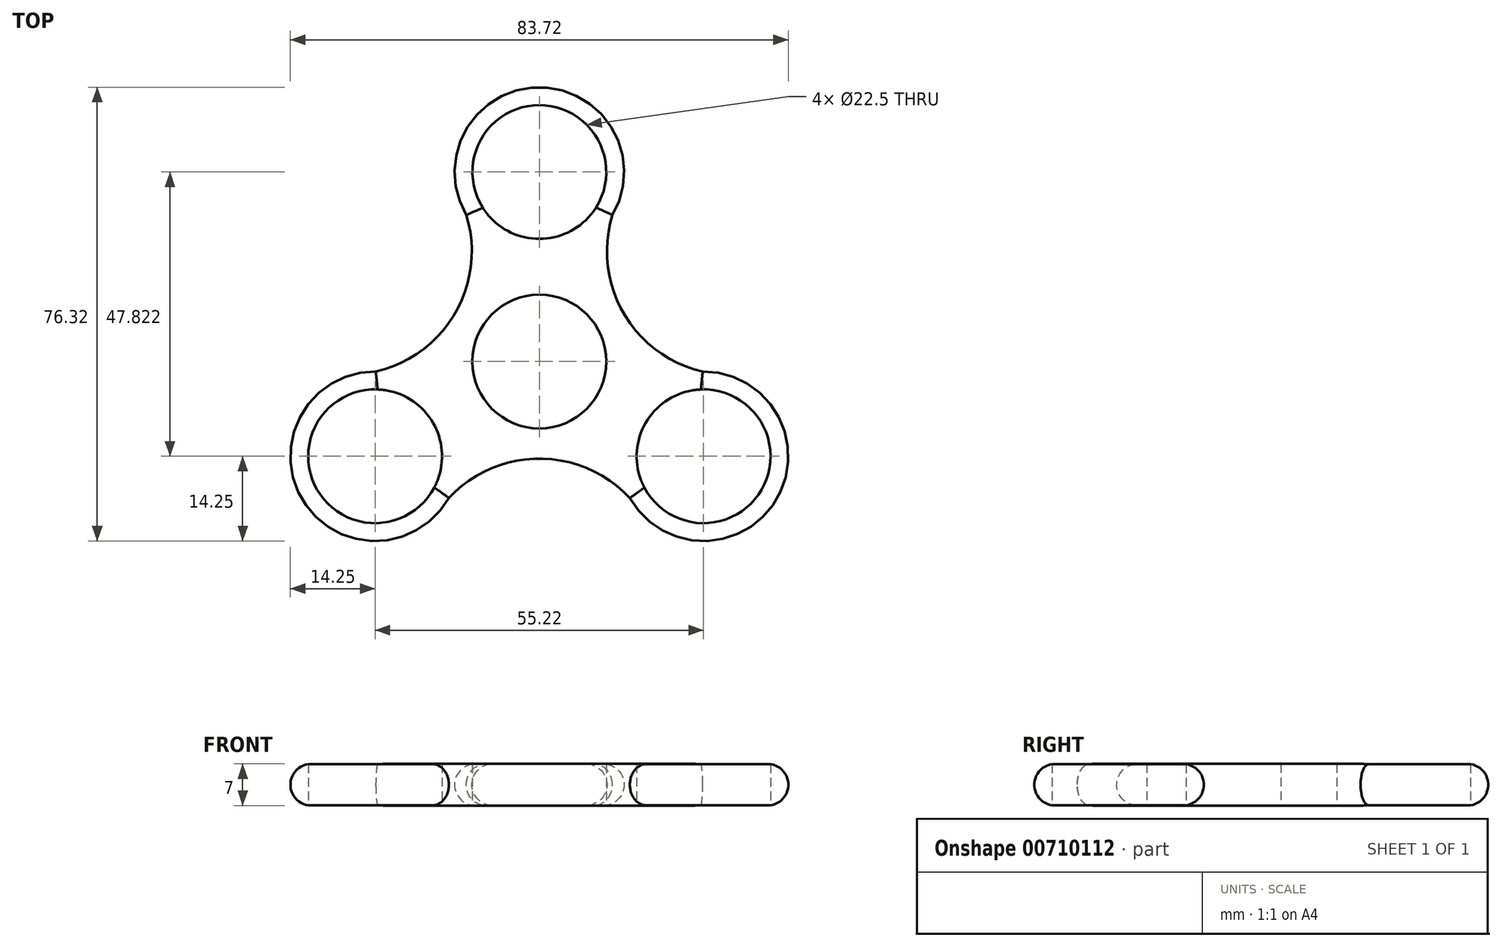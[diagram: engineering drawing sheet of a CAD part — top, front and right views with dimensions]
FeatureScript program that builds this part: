
annotation { "Feature Type Name" : "Feature", "Feature Type Description" : "" }
export const myFeature = defineFeature(function(context is Context, id is Id, definition is map)
    precondition{}
    {
        {
            var Q0;
            Q0=qCreatedBy(makeId("Top.planeOp"),FACE);
            var sketch = newSketch(context, id + "F0", { "sketchPlane" : qUnion([Q0])});
            skCircle(sketch, "E0", {"center": v(0, 0) * mm, "radius": 11.25 * mm});
            skCircle(sketch, "E1", {"center": v(0, 31.88) * mm, "radius": 11.25 * mm});
            skArc(sketch, "E2", {"start": v(12.29, 24.67) * mm, "mid": v(-0.02, 46.13) * mm, "end": v(-12.27, 24.64) * mm});
            skArc(sketch, "E3.1.0", {"start": v(-27.5, -1.7) * mm, "mid": v(-39.94, -23.08) * mm, "end": v(-15.2, -22.94) * mm});
            skCircle(sketch, "E3.1.1", {"center": v(-27.6, -15.94) * mm, "radius": 11.25 * mm});
            skArc(sketch, "E3.2.0", {"start": v(15.22, -22.98) * mm, "mid": v(39.96, -23.05) * mm, "end": v(27.47, -1.7) * mm});
            skCircle(sketch, "E3.2.1", {"center": v(27.6, -15.94) * mm, "radius": 11.25 * mm});
            skArc(sketch, "E4", {"start": v(13.79, 28.28) * mm, "mid": v(13.24, 9.92) * mm, "end": v(27.47, -1.7) * mm});
            skArc(sketch, "E5.1.0", {"start": v(-31.39, -2.2) * mm, "mid": v(-15.22, 6.5) * mm, "end": v(-12.27, 24.64) * mm});
            skArc(sketch, "E5.2.0", {"start": v(17.6, -26.08) * mm, "mid": v(1.97, -16.43) * mm, "end": v(-15.2, -22.94) * mm});
            skSolve(sketch);
        }
        {
            var Q0;
            Q0 = qSketchRegion(id + "F0", true);
            extrude(context, id + "F1", {"entities" : qUnion([Q0]), "depth" : 7 * mm, "offsetDistance" : 25 * mm});
        }
        {
            var Q0;
            Q0=makeQuery(id+"F1.opExtrude","CAP_EDGE",EDGE,{"disambiguationData":[OSD([sQuery(id+"F0.wireOp",EDGE,"E5.1.0")])],"isStart":false});
            var Q1;
            Q1=makeQuery(id+"F1.opExtrude","CAP_EDGE",EDGE,{"disambiguationData":[OSD([sQuery(id+"F0.wireOp",EDGE,"E5.1.0")])],"isStart":true});
            var Q2;
            Q2=makeQuery(id+"F1.opExtrude","CAP_EDGE",EDGE,{"disambiguationData":[OSD([sQuery(id+"F0.wireOp",EDGE,"E2")])],"isStart":false});
            var Q3;
            Q3=makeQuery(id+"F1.opExtrude","CAP_EDGE",EDGE,{"disambiguationData":[OSD([sQuery(id+"F0.wireOp",EDGE,"E4")])],"isStart":false});
            var Q4;
            Q4=makeQuery(id+"F1.opExtrude","CAP_EDGE",EDGE,{"disambiguationData":[OSD([sQuery(id+"F0.wireOp",EDGE,"E3.2.0")])],"isStart":false});
            var Q5;
            Q5=makeQuery(id+"F1.opExtrude","CAP_EDGE",EDGE,{"disambiguationData":[OSD([sQuery(id+"F0.wireOp",EDGE,"E5.2.0")])],"isStart":false});
            var Q6;
            Q6=makeQuery(id+"F1.opExtrude","CAP_EDGE",EDGE,{"disambiguationData":[OSD([sQuery(id+"F0.wireOp",EDGE,"E3.1.0")])],"isStart":false});
            var Q7;
            Q7=makeQuery(id+"F1.opExtrude","CAP_EDGE",EDGE,{"disambiguationData":[OSD([sQuery(id+"F0.wireOp",EDGE,"E2")])],"isStart":true});
            var Q8;
            Q8=makeQuery(id+"F1.opExtrude","CAP_EDGE",EDGE,{"disambiguationData":[OSD([sQuery(id+"F0.wireOp",EDGE,"E4")])],"isStart":true});
            var Q9;
            Q9=makeQuery(id+"F1.opExtrude","CAP_EDGE",EDGE,{"disambiguationData":[OSD([sQuery(id+"F0.wireOp",EDGE,"E3.2.0")])],"isStart":true});
            var Q10;
            Q10=makeQuery(id+"F1.opExtrude","CAP_EDGE",EDGE,{"disambiguationData":[OSD([sQuery(id+"F0.wireOp",EDGE,"E5.2.0")])],"isStart":true});
            var Q11;
            Q11=makeQuery(id+"F1.opExtrude","CAP_EDGE",EDGE,{"disambiguationData":[OSD([sQuery(id+"F0.wireOp",EDGE,"E3.1.0")])],"isStart":true});
            fillet(context, id + "F2", {"entities" : qUnion([Q0, Q1, Q2, Q3, Q4, Q5, Q6, Q7, Q8, Q9, Q10, Q11]), "radius" : 3.5 * mm, "tangentPropagation" : true, "allowEdgeOverflow" : false});
        }
    });
